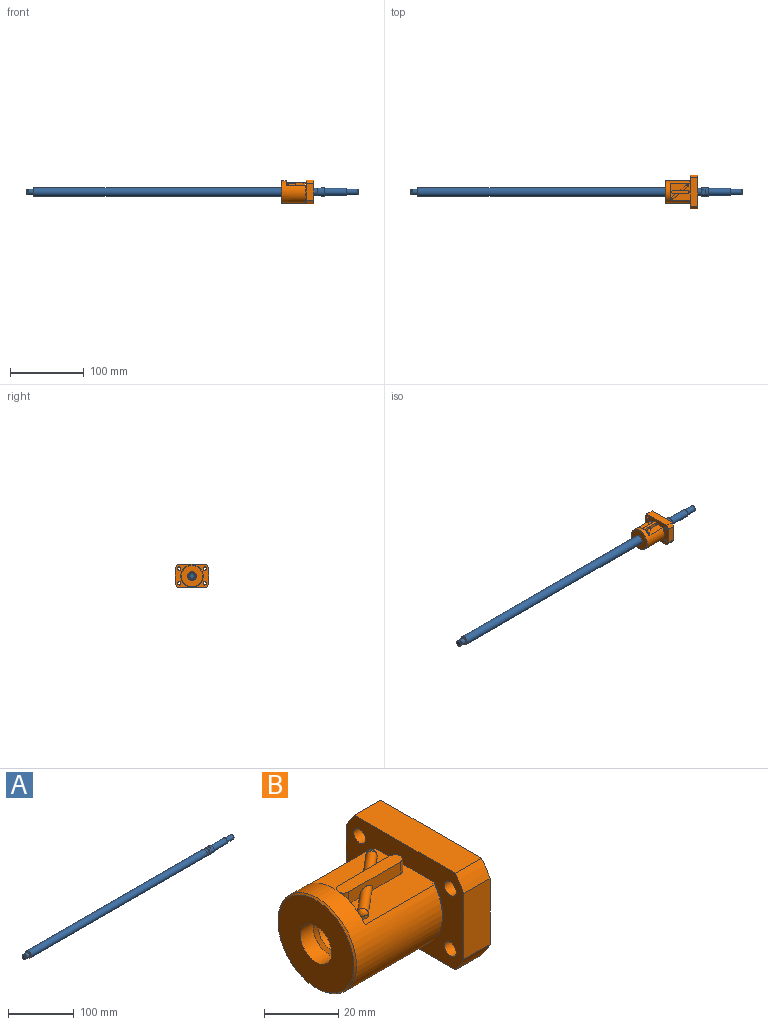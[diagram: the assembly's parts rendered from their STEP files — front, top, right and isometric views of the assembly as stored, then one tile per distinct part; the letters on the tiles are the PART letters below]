
ASSEMBLY  parts=2 mates=1
PART A: 29 faces, bbox 450x12x12 mm
  f0: cylinder r=6mm len=12mm, axis (-1,0,0), area 299.2mm2, adj f1,f2,f8,f25,f26,f27,f28
  f1: plane 10x6mm, normal (-1,0,0), area 12.8mm2, adj f0,f9,f25,f28
  f2: plane 10x6mm, normal (-1,0,0), area 12.8mm2, adj f0,f9,f25,f28
  f3: cylinder r=4mm len=8mm, axis (-1,0,0), area 170.9mm2, adj f16,f21
  f4: cylinder r=6mm len=379.5mm, axis (-1,0,0), area 14306.8mm2, adj f10,f18
  f5: cylinder r=5mm len=29.3mm, axis (-1,0,0), area 920.5mm2, adj f6,f11
  f6: torus R=5.2mm, axis (-1,0,0), area 10mm2, adj f5,f7
  f7: plane 11.6x11.6mm, normal (1,0,0), area 20.7mm2, adj f6,f8
  f8: cone r=5.8mm half-angle=45deg, axis (-1,0,0), area 10.5mm2, adj f0,f7
  f9: cylinder r=5mm len=10mm, axis (-1,0,0), area 157.1mm2, adj f1,f2,f10
  f10: plane 12x12mm, normal (1,0,0), area 34.6mm2, adj f4,f9
  f11: cone r=5mm half-angle=45deg, axis (-1,0,0), area 21.1mm2, adj f5,f15
  f12: plane 7x7mm, normal (1,0,0), area 38.5mm2, adj f13
  f13: cone r=3.5mm half-angle=45deg, axis (-1,0,0), area 16.7mm2, adj f12,f14
  f14: cylinder r=4mm len=14.5mm, axis (-1,0,0), area 364.4mm2, adj f13,f15
  f15: plane 9x9mm, normal (1,0,0), area 13.4mm2, adj f11,f14
  f16: torus R=4.2mm, axis (-1,0,0), area 8mm2, adj f3,f17
  f17: plane 11x11mm, normal (-1,0,0), area 39.6mm2, adj f16,f18
  f18: cone r=5.5mm half-angle=45deg, axis (1,0,0), area 25.5mm2, adj f4,f17
  f19: plane 8x8mm, normal (1,0,0), area 4.9mm2, adj f20,f24
  f20: cylinder r=3.8mm len=7.6mm, axis (-1,0,0), area 21.5mm2, adj f19,f21
  f21: plane 8x8mm, normal (-1,0,0), area 4.9mm2, adj f3,f20
  f22: plane 7x7mm, normal (-1,0,0), area 38.5mm2, adj f23
  f23: cone r=3.5mm half-angle=45deg, axis (1,0,0), area 16.7mm2, adj f22,f24
  f24: cylinder r=4mm len=8mm, axis (-1,0,0), area 40.2mm2, adj f19,f23
  f25: plane 6.63x5mm, normal (0,0,-1), area 33.2mm2, adj f0,f1,f2,f26
  f26: plane 6.63x1mm, normal (-1,0,0), area 4.5mm2, adj f0,f25
  f27: plane 6.63x1mm, normal (-1,0,0), area 4.5mm2, adj f0,f28
  f28: plane 6.63x5mm, normal (0,0,1), area 33.2mm2, adj f0,f1,f2,f27
PART B: 45 faces, bbox 44x45x32 mm
  f0: plane 29x29mm, normal (-1,0,0), area 547.4mm2, adj f13,f40
  f1: plane 45x32mm, normal (1,0,0), area 1095.3mm2, adj f18,f19,f20,f21,f22,f23,f24,f25
  f2: plane 27.2x24mm, normal (0,0,1), area 505.4mm2, adj f4,f5,f7,f8,f14,f15,f16,f17
  f3: sphere r=1.5mm, area 7.1mm2, adj f4,f39
  f4: cylinder r=1.5mm len=11.26mm, axis (-0.77,-0.64,0), area 70.6mm2, adj f2,f3,f7,f39
  f5: cylinder r=1.5mm len=11.26mm, axis (-0.77,-0.64,0), area 70.6mm2, adj f2,f6,f8,f38
  f6: sphere r=1.5mm, area 7.1mm2, adj f5,f38
  f7: plane 19.8x4mm, normal (0,-1,0), area 69.4mm2, adj f2,f4,f35,f36,f37
  f8: plane 19.8x4mm, normal (0,1,0), area 69.4mm2, adj f2,f5,f35,f36,f37
  f9: cylinder r=2.25mm len=5.6mm, axis (-1,0,0), area 79.2mm2, adj f17,f33
  f10: cylinder r=2.25mm len=5.6mm, axis (-1,0,0), area 79.2mm2, adj f17,f31
  f11: cylinder r=2.25mm len=5.6mm, axis (-1,0,0), area 79.2mm2, adj f17,f29
  f12: cylinder r=2.25mm len=5.6mm, axis (-1,0,0), area 79.2mm2, adj f17,f27
  f13: cone r=15mm half-angle=45deg, axis (1,0,0), area 65.5mm2, adj f0,f14
  f14: cylinder r=15mm len=32.82mm, axis (-1,0,0), area 2355.5mm2, adj f2,f13,f15,f34
  f15: plane 30x24mm, normal (1,0,0), area 39.3mm2, adj f2,f14,f16
  f16: cylinder r=14.4mm len=28.8mm, axis (-1,0,0), area 44mm2, adj f2,f15,f17
  f17: plane 45x32mm, normal (-1,0,0), area 778.9mm2, adj f2,f9,f10,f11,f12,f16,f18,f19
  f18: cylinder r=25mm len=10mm, axis (-1,0,0), area 60.9mm2, adj f1,f17,f19,f25
  f19: plane 38.42x10mm, normal (0,0,1), area 384.2mm2, adj f1,f17,f18,f20
  f20: cylinder r=25mm len=10mm, axis (-1,0,0), area 60.9mm2, adj f1,f17,f19,f21
  f21: plane 21.79x10mm, normal (0,-1,0), area 217.9mm2, adj f1,f17,f20,f22
  f22: cylinder r=25mm len=10mm, axis (-1,0,0), area 60.9mm2, adj f1,f17,f21,f23
  f23: plane 38.42x10mm, normal (0,0,-1), area 384.2mm2, adj f1,f17,f22,f24
  f24: cylinder r=25mm len=10mm, axis (-1,0,0), area 60.9mm2, adj f1,f17,f23,f25
  f25: plane 21.79x10mm, normal (0,1,0), area 217.9mm2, adj f1,f17,f18,f24
  f26: cylinder r=4mm len=8mm, axis (1,0,0), area 110.6mm2, adj f1,f27
  f27: plane 8x8mm, normal (1,0,0), area 34.4mm2, adj f12,f26
  f28: cylinder r=4mm len=8mm, axis (1,0,0), area 110.6mm2, adj f1,f29
  f29: plane 8x8mm, normal (1,0,0), area 34.4mm2, adj f11,f28
  f30: cylinder r=4mm len=8mm, axis (1,0,0), area 110.6mm2, adj f1,f31
  f31: plane 8x8mm, normal (1,0,0), area 34.4mm2, adj f10,f30
  f32: cylinder r=4mm len=8mm, axis (1,0,0), area 110.6mm2, adj f1,f33
  f33: plane 8x8mm, normal (1,0,0), area 34.4mm2, adj f9,f32
  f34: plane 24x6mm, normal (1,0,0), area 100.6mm2, adj f2,f14
  f35: cylinder r=2mm len=4mm, axis (0,0,-1), area 25.1mm2, adj f2,f7,f8,f37
  f36: cylinder r=2mm len=4mm, axis (0,0,-1), area 25.1mm2, adj f2,f7,f8,f37
  f37: plane 23.8x4mm, normal (0,0,1), area 91.8mm2, adj f7,f8,f35,f36
  f38: cylinder r=1.5mm len=3mm, axis (0,0,1), area 5.8mm2, adj f2,f5,f6
  f39: cylinder r=1.5mm len=3mm, axis (0,0,1), area 5.8mm2, adj f2,f3,f4
  f40: cylinder r=6mm len=12mm, axis (-1,0,0), area 188.5mm2, adj f0,f41
  f41: cone r=5.05mm half-angle=45deg, axis (-1,0,0), area 46.5mm2, adj f40,f42
  f42: cylinder r=5.05mm len=32.11mm, axis (-1,0,0), area 1019.3mm2, adj f41,f43
  f43: cone r=6mm half-angle=45deg, axis (1,0,0), area 46.5mm2, adj f42,f44
  f44: cylinder r=6mm len=12mm, axis (-1,0,0), area 188.5mm2, adj f1,f43
PLACE A at identity
PLACE B t=(346,0,0)mm
MATE cylindrical B.f13 <-> A.f0  axis (1,0,0) through (390,0,0)mm
